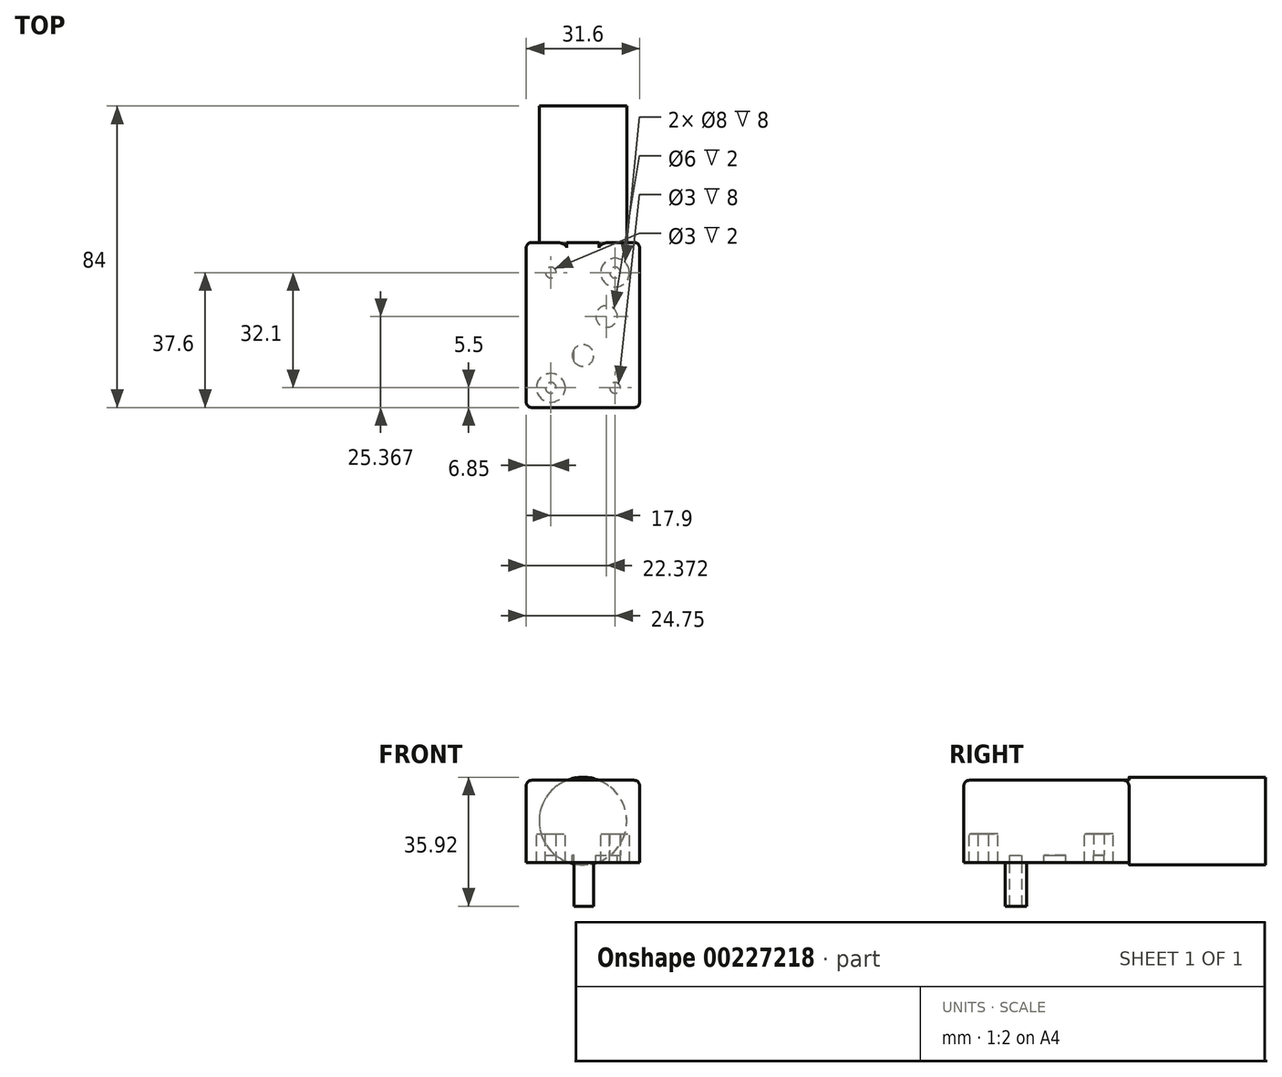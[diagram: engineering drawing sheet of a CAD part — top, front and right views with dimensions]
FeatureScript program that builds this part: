
annotation { "Feature Type Name" : "Feature", "Feature Type Description" : "" }
export const myFeature = defineFeature(function(context is Context, id is Id, definition is map)
    precondition{}
    {
        {
            var Q0;
            Q0=qCreatedBy(makeId("Top.planeOp"),FACE);
            var sketch = newSketch(context, id + "F0", { "sketchPlane" : qUnion([Q0])});
            skLineSegment(sketch, "E0.bottom", {"start": v(15.8, 23) * mm, "end": v(-15.8, 23) * mm});
            skLineSegment(sketch, "E0.top", {"start": v(15.8, -23) * mm, "end": v(-15.8, -23) * mm});
            skLineSegment(sketch, "E0.left", {"start": v(15.8, 23) * mm, "end": v(15.8, -23) * mm});
            skLineSegment(sketch, "E0.right", {"start": v(-15.8, 23) * mm, "end": v(-15.8, -23) * mm});
            skPoint(sketch, "E0.middle", {"position": v(0, 0) * mm});
            skSolve(sketch);
        }
        {
            var Q0;
            Q0 = qSketchRegion(id + "F0", true);
            extrude(context, id + "F1", {"entities" : qUnion([Q0]), "depth" : 20.9 * mm});
        }
        {
            var Q0;
            Q0=makeQuery(id+"F1.opExtrude","SWEPT_FACE",FACE,{"disambiguationData":[OSD([sQuery(id+"F0.wireOp",EDGE,"E0.bottom")])]});
            var sketch = newSketch(context, id + "F2", { "sketchPlane" : qUnion([Q0])});
            skCircle(sketch, "E1", {"center": v(0, 9.55) * mm, "radius": 12.2 * mm});
            skSolve(sketch);
        }
        {
            var Q0;
            Q0 = qSketchRegion(id + "F2", true);
            extrude(context, id + "F3", {"entities" : qUnion([Q0]), "operationType" : NewBodyOperationType.ADD, "depth" : 38 * mm});
        }
        {
            var Q0;
            Q0=makeQuery(id+"F1.opExtrude","CAP_FACE",FACE,{"disambiguationData":[OSD([sQuery(id+"F0.wireOp",EDGE,"E0.bottom"),sQuery(id+"F0.wireOp",EDGE,"E0.top"),sQuery(id+"F0.wireOp",EDGE,"E0.left"),sQuery(id+"F0.wireOp",EDGE,"E0.right")])],"isStart":true});
            var sketch = newSketch(context, id + "F4", { "sketchPlane" : qUnion([Q0])});
            skCircle(sketch, "E2", {"center": v(0, 8.5) * mm, "radius": 3 * mm});
            skCircle(sketch, "E3", {"center": v(0, 8.5) * mm, "radius": 7.5 * mm});
            skLineSegment(sketch, "E4", {"start": v(3, 8.5) * mm, "end": v(-2.5, 8.5) * mm});
            skLineSegment(sketch, "E5", {"start": v(-2.5, 10.16) * mm, "end": v(-2.5, 6.84) * mm});
            skCircle(sketch, "E6", {"center": v(8.95, 17.5) * mm, "radius": 4 * mm});
            skCircle(sketch, "E7", {"center": v(8.95, 17.5) * mm, "radius": 1.5 * mm});
            skLineSegment(sketch, "E8", {"start": v(0, 23) * mm, "end": v(0, 18.4) * mm});
            skPoint(sketch, "E8.endSnap0", {"position": v(0, 23) * mm});
            skCircle(sketch, "E9.MirrorC", {"center": v(-8.95, 17.5) * mm, "radius": 1.5 * mm});
            skCircle(sketch, "E10.MirrorC", {"center": v(-8.95, 17.5) * mm, "radius": 4 * mm});
            skCircle(sketch, "E11", {"center": v(-6.57, -2.37) * mm, "radius": 3 * mm});
            skCircle(sketch, "E12.MirrorC", {"center": v(6.57, -2.37) * mm, "radius": 3 * mm});
            skCircle(sketch, "E13", {"center": v(-8.95, -14.6) * mm, "radius": 4 * mm});
            skCircle(sketch, "E14.MirrorC", {"center": v(8.95, -14.6) * mm, "radius": 4 * mm});
            skCircle(sketch, "E15", {"center": v(-8.95, -14.6) * mm, "radius": 1.5 * mm});
            skCircle(sketch, "E16.MirrorC", {"center": v(8.95, -14.6) * mm, "radius": 1.5 * mm});
            skLineSegment(sketch, "E17", {"start": v(-15.8, 23) * mm, "end": v(15.8, 23) * mm});
            skLineSegment(sketch, "E18", {"start": v(15.8, 23) * mm, "end": v(15.8, -23) * mm});
            skLineSegment(sketch, "E19", {"start": v(-12.95, 17.5) * mm, "end": v(12.95, 17.5) * mm});
            skLineSegment(sketch, "E20", {"start": v(8.95, 21.5) * mm, "end": v(8.95, -18.6) * mm});
            skLineSegment(sketch, "E21", {"start": v(12.95, -14.6) * mm, "end": v(-12.95, -14.6) * mm});
            skLineSegment(sketch, "E22", {"start": v(-8.95, -18.6) * mm, "end": v(-8.95, 21.5) * mm});
            skLineSegment(sketch, "E23", {"start": v(0, 23) * mm, "end": v(0, 16) * mm});
            skPoint(sketch, "E23.endSnap0", {"position": v(0, 17.5) * mm});
            skSolve(sketch);
        }
        {
            var Q0;
            Q0=makeQuery(id+"F4.imprint","IMPRINT",FACE,{"disambiguationData":[TD([[makeQuery(id+"F4.imprint","IMPRINT",EDGE,{"derivedFrom":sQuery(id+"F4.wireOp",EDGE,"E3")}),1.0]])]});
            var Q1;
            Q1=makeQuery(id+"F4.imprint","IMPRINT",FACE,{"disambiguationData":[TD([[makeQuery(id+"F4.imprint","IMPRINT",EDGE,{"derivedFrom":sQuery(id+"F4.wireOp",EDGE,"E6")}),1.0]])]});
            var Q2;
            Q2=makeQuery(id+"F4.imprint","IMPRINT",FACE,{"disambiguationData":[TD([[makeQuery(id+"F4.imprint","IMPRINT",EDGE,{"derivedFrom":sQuery(id+"F4.wireOp",EDGE,"E9.MirrorC")}),1.0]])]});
            var Q3;
            Q3=makeQuery(id+"F4.imprint","IMPRINT",FACE,{"disambiguationData":[TD([[makeQuery(id+"F4.imprint","IMPRINT",EDGE,{"derivedFrom":sQuery(id+"F4.wireOp",EDGE,"E11")}),1.0]])]});
            var Q4;
            Q4=makeQuery(id+"F4.imprint","IMPRINT",FACE,{"disambiguationData":[TD([[makeQuery(id+"F4.imprint","IMPRINT",EDGE,{"derivedFrom":sQuery(id+"F4.wireOp",EDGE,"E12.MirrorC")}),-1.0]])]});
            var Q5;
            Q5=makeQuery(id+"F4.imprint","IMPRINT",FACE,{"disambiguationData":[TD([[makeQuery(id+"F4.imprint","IMPRINT",EDGE,{"derivedFrom":sQuery(id+"F4.wireOp",EDGE,"E14.MirrorC")}),-1.0]])]});
            var Q6;
            {var subQ0=sQuery(id+"F4.wireOp",EDGE,"NOkgakyG-LXeg-HDE5-BnBK-bHET0c2Zb8rj");var subQ1=sQuery(id+"F4.wireOp",EDGE,"E13");var subQ2=makeQuery(id+"F4.imprint","INTERSECT",VERTEX,{"disambiguationData":[OD(0.0)],"derivedFrom":[subQ1,subQ0]});Q6=makeQuery(id+"F4.imprint","IMPRINT",FACE,{"disambiguationData":[TD([[makeQuery(id+"F4.imprint","IMPRINT",EDGE,{"disambiguationData":[TD([[subQ2,1.0]])],"derivedFrom":subQ1}),-1.0]])]});}
            var Q7;
            Q7=makeQuery(id+"F4.imprint","IMPRINT",FACE,{"disambiguationData":[TD([[makeQuery(id+"F4.imprint","IMPRINT",EDGE,{"derivedFrom":sQuery(id+"F4.wireOp",EDGE,"E15")}),-1.0]])]});
            var Q8;
            {var subQ0=sQuery(id+"F4.wireOp",EDGE,"1uIMe50a-NhlS-mpyl-1LAA-AuPrayMO8yyJ");var subQ1=sQuery(id+"F4.wireOp",EDGE,"E13");var subQ2=makeQuery(id+"F4.imprint","INTERSECT",VERTEX,{"disambiguationData":[OD(0.0)],"derivedFrom":[subQ1,subQ0]});Q8=makeQuery(id+"F4.imprint","IMPRINT",FACE,{"disambiguationData":[TD([[makeQuery(id+"F4.imprint","IMPRINT",EDGE,{"disambiguationData":[TD([[subQ2,1.0]])],"derivedFrom":subQ1}),1.0]])]});}
            var Q9;
            {var subQ0=sQuery(id+"F4.wireOp",EDGE,"E5");var subQ1=sQuery(id+"F4.wireOp",EDGE,"E2");var subQ2=makeQuery(id+"F4.imprint","INTERSECT",VERTEX,{"disambiguationData":[OD(0.0)],"derivedFrom":[subQ1,subQ0]});Q9=makeQuery(id+"F4.imprint","IMPRINT",FACE,{"disambiguationData":[TD([[makeQuery(id+"F4.imprint","IMPRINT",EDGE,{"disambiguationData":[TD([[subQ2,-1.0]])],"derivedFrom":subQ1}),1.0]])]});}
            var Q10;
            {var subQ3=sQuery(id+"F4.wireOp",EDGE,"hSGFdUEP-K8hc-nEsh-8xql-g1AnP8qAutbP.top");var subQ5=sQuery(id+"F4.wireOp",EDGE,"E13");var subQ8=makeQuery(id+"F4.imprint","INTERSECT",VERTEX,{"derivedFrom":[subQ5,subQ3]});Q10=makeQuery(id+"F4.imprint","IMPRINT",FACE,{"disambiguationData":[TD([[makeQuery(id+"F4.imprint","IMPRINT",EDGE,{"disambiguationData":[TD([[subQ8,1.0]])],"derivedFrom":subQ5}),1.0]])]});}
            var Q11;
            {var subQ0=sQuery(id+"F4.wireOp",EDGE,"hSGFdUEP-K8hc-nEsh-8xql-g1AnP8qAutbP.left");var subQ1=sQuery(id+"F4.wireOp",EDGE,"E13");var subQ2=makeQuery(id+"F4.imprint","INTERSECT",VERTEX,{"derivedFrom":[subQ1,subQ0]});Q11=makeQuery(id+"F4.imprint","IMPRINT",FACE,{"disambiguationData":[TD([[makeQuery(id+"F4.imprint","IMPRINT",EDGE,{"disambiguationData":[TD([[subQ2,-1.0]])],"derivedFrom":subQ1}),1.0]])]});}
            var Q12;
            {var subQ3=sQuery(id+"F4.wireOp",EDGE,"1uIMe50a-NhlS-mpyl-1LAA-AuPrayMO8yyJ");var subQ6=sQuery(id+"F4.wireOp",EDGE,"E13");var subQ9=makeQuery(id+"F4.imprint","INTERSECT",VERTEX,{"disambiguationData":[OD(0.0)],"derivedFrom":[subQ6,subQ3]});Q12=makeQuery(id+"F4.imprint","IMPRINT",FACE,{"disambiguationData":[TD([[makeQuery(id+"F4.imprint","IMPRINT",EDGE,{"disambiguationData":[TD([[subQ9,-1.0]])],"derivedFrom":subQ6}),1.0]])]});}
            extrude(context, id + "F5", {"entities" : qUnion([Q0, Q1, Q2, Q3, Q4, Q5, Q6, Q7, Q8, Q9, Q10, Q11, Q12]), "operationType" : NewBodyOperationType.ADD, "depth" : 2 * mm});
        }
        {
            var Q0;
            {var subQ0=sQuery(id+"F4.wireOp",EDGE,"E4");Q0=makeQuery(id+"F4.imprint","IMPRINT",FACE,{"disambiguationData":[TD([[makeQuery(id+"F4.imprint","IMPRINT",EDGE,{"derivedFrom":subQ0}),-1.0]])]});}
            var Q1;
            {var subQ0=sQuery(id+"F4.wireOp",EDGE,"E4");Q1=makeQuery(id+"F4.imprint","IMPRINT",FACE,{"disambiguationData":[TD([[makeQuery(id+"F4.imprint","IMPRINT",EDGE,{"derivedFrom":subQ0}),1.0]])]});}
            extrude(context, id + "F6", {"entities" : qUnion([Q0, Q1]), "operationType" : NewBodyOperationType.ADD, "depth" : 14.17 * mm});
        }
        {
            var Q0;
            {var subQ0=sQuery(id+"F4.wireOp",EDGE,"1uIMe50a-NhlS-mpyl-1LAA-AuPrayMO8yyJ");var subQ1=sQuery(id+"F4.wireOp",EDGE,"E15");var subQ2=makeQuery(id+"F4.imprint","INTERSECT",VERTEX,{"disambiguationData":[OD(0.0)],"derivedFrom":[subQ1,subQ0]});Q0=makeQuery(id+"F4.imprint","IMPRINT",FACE,{"disambiguationData":[TD([[makeQuery(id+"F4.imprint","IMPRINT",EDGE,{"disambiguationData":[TD([[subQ2,1.0]])],"derivedFrom":subQ1}),1.0]])]});}
            var Q1;
            Q1=makeQuery(id+"F4.imprint","IMPRINT",FACE,{"disambiguationData":[TD([[makeQuery(id+"F4.imprint","IMPRINT",EDGE,{"derivedFrom":sQuery(id+"F4.wireOp",EDGE,"E16.MirrorC")}),-1.0]])]});
            var Q2;
            Q2=makeQuery(id+"F4.imprint","IMPRINT",FACE,{"disambiguationData":[TD([[makeQuery(id+"F4.imprint","IMPRINT",EDGE,{"derivedFrom":sQuery(id+"F4.wireOp",EDGE,"E7")}),1.0]])]});
            var Q3;
            Q3=makeQuery(id+"F4.imprint","IMPRINT",FACE,{"disambiguationData":[TD([[makeQuery(id+"F4.imprint","IMPRINT",EDGE,{"derivedFrom":sQuery(id+"F4.wireOp",EDGE,"E9.MirrorC")}),-1.0]])]});
            var Q4;
            {var subQ0=sQuery(id+"F4.wireOp",EDGE,"1uIMe50a-NhlS-mpyl-1LAA-AuPrayMO8yyJ");var subQ1=sQuery(id+"F4.wireOp",EDGE,"E15");var subQ2=makeQuery(id+"F4.imprint","INTERSECT",VERTEX,{"disambiguationData":[OD(0.0)],"derivedFrom":[subQ1,subQ0]});Q4=makeQuery(id+"F4.imprint","IMPRINT",FACE,{"disambiguationData":[TD([[makeQuery(id+"F4.imprint","IMPRINT",EDGE,{"disambiguationData":[TD([[subQ2,-1.0]])],"derivedFrom":subQ1}),1.0]])]});}
            extrude(context, id + "F7", {"entities" : qUnion([Q0, Q1, Q2, Q3, Q4]), "operationType" : NewBodyOperationType.REMOVE, "oppositeDirection" : true, "depth" : 6 * mm});
        }
        {
            var Q0;
            Q0=makeQuery(id+"F1.opExtrude","CAP_EDGE",EDGE,{"disambiguationData":[OSD([sQuery(id+"F0.wireOp",EDGE,"E0.left")])],"isStart":false});
            var Q1;
            Q1=makeQuery(id+"F1.opExtrude","SWEPT_EDGE",EDGE,{"disambiguationData":[OSD([sQuery(id+"F0.wireOp",EDGE,"E0.bottom"),sQuery(id+"F0.wireOp",EDGE,"E0.left")])]});
            var Q2;
            {var subQ1=sQuery(id+"F0.wireOp",EDGE,"E0.left");var subQ2=sQuery(id+"F0.wireOp",EDGE,"E0.bottom");var subQ3=makeQuery(id+"F1.opExtrude","CAP_FACE",FACE,{"disambiguationData":[OSD([subQ2,sQuery(id+"F0.wireOp",EDGE,"E0.top"),subQ1,sQuery(id+"F0.wireOp",EDGE,"E0.right")])],"isStart":false});var subQ4=makeQuery(id+"F1.opExtrude","SWEPT_FACE",FACE,{"disambiguationData":[OSD([subQ2])]});Q2=makeQuery(id+"F3.boolean.opBoolean","SPLIT",EDGE,{"disambiguationData":[topologyDisambiguationEdgeConnected([subQ4,subQ3]),TD([makeQuery(id+"F1.opExtrude","SWEPT_FACE",FACE,{"disambiguationData":[OSD([subQ1])]})])],"derivedFrom":makeQuery(id+"F1.opExtrude","CAP_EDGE",EDGE,{"disambiguationData":[OSD([subQ2])],"isStart":false})});}
            var Q3;
            {var subQ1=sQuery(id+"F0.wireOp",EDGE,"E0.right");var subQ2=sQuery(id+"F0.wireOp",EDGE,"E0.bottom");var subQ3=makeQuery(id+"F1.opExtrude","CAP_FACE",FACE,{"disambiguationData":[OSD([subQ2,sQuery(id+"F0.wireOp",EDGE,"E0.top"),sQuery(id+"F0.wireOp",EDGE,"E0.left"),subQ1])],"isStart":false});var subQ4=makeQuery(id+"F1.opExtrude","SWEPT_FACE",FACE,{"disambiguationData":[OSD([subQ2])]});Q3=makeQuery(id+"F3.boolean.opBoolean","SPLIT",EDGE,{"disambiguationData":[topologyDisambiguationEdgeConnected([subQ4,subQ3]),TD([makeQuery(id+"F1.opExtrude","SWEPT_FACE",FACE,{"disambiguationData":[OSD([subQ1])]})])],"derivedFrom":makeQuery(id+"F1.opExtrude","CAP_EDGE",EDGE,{"disambiguationData":[OSD([subQ2])],"isStart":false})});}
            var Q4;
            Q4=makeQuery(id+"F1.opExtrude","CAP_EDGE",EDGE,{"disambiguationData":[OSD([sQuery(id+"F0.wireOp",EDGE,"E0.right")])],"isStart":false});
            var Q5;
            Q5=makeQuery(id+"F1.opExtrude","SWEPT_EDGE",EDGE,{"disambiguationData":[OSD([sQuery(id+"F0.wireOp",EDGE,"E0.bottom"),sQuery(id+"F0.wireOp",EDGE,"E0.right")])]});
            var Q6;
            Q6=makeQuery(id+"F1.opExtrude","SWEPT_EDGE",EDGE,{"disambiguationData":[OSD([sQuery(id+"F0.wireOp",EDGE,"E0.top"),sQuery(id+"F0.wireOp",EDGE,"E0.right")])]});
            var Q7;
            Q7=makeQuery(id+"F1.opExtrude","CAP_EDGE",EDGE,{"disambiguationData":[OSD([sQuery(id+"F0.wireOp",EDGE,"E0.top")])],"isStart":false});
            var Q8;
            Q8=makeQuery(id+"F1.opExtrude","SWEPT_EDGE",EDGE,{"disambiguationData":[OSD([sQuery(id+"F0.wireOp",EDGE,"E0.top"),sQuery(id+"F0.wireOp",EDGE,"E0.left")])]});
            fillet(context, id + "F8", {"entities" : qUnion([Q0, Q1, Q2, Q3, Q4, Q5, Q6, Q7, Q8]), "radius" : 1.5 * mm, "tangentPropagation" : true, "allowEdgeOverflow" : false});
        }
    });
